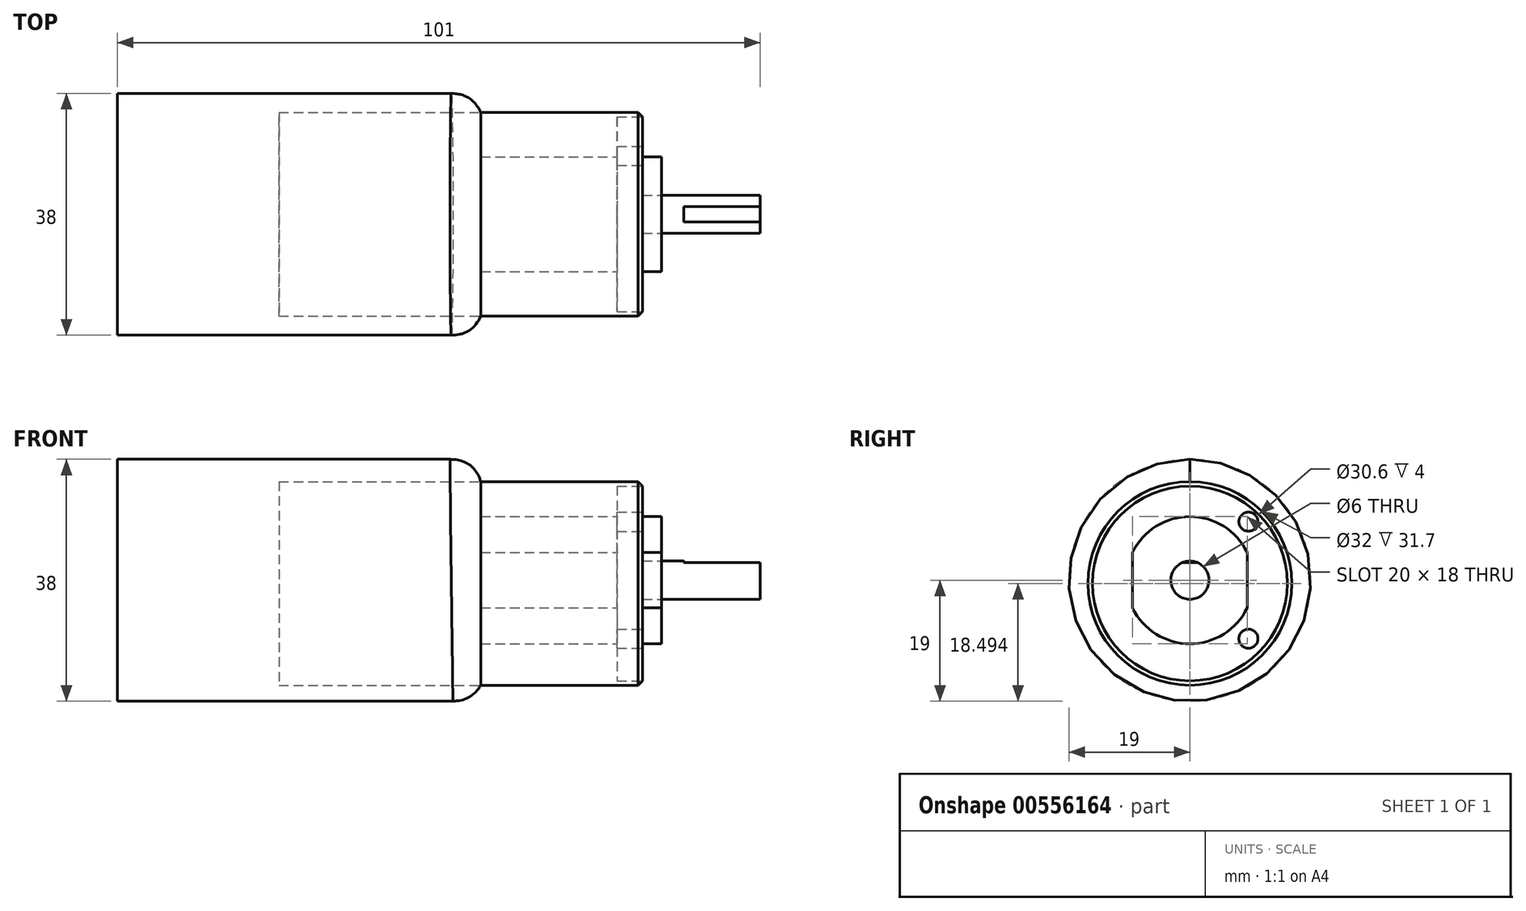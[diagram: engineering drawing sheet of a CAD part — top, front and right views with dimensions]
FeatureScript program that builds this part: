
annotation { "Feature Type Name" : "Feature", "Feature Type Description" : "" }
export const myFeature = defineFeature(function(context is Context, id is Id, definition is map)
    precondition{}
    {
        {
            var Q0;
            Q0=qCreatedBy(makeId("Right.planeOp"),FACE);
            var sketch = newSketch(context, id + "F0", { "sketchPlane" : qUnion([Q0])});
            skCircle(sketch, "E0", {"center": v(0, 0) * mm, "radius": 3 * mm});
            skSolve(sketch);
        }
        {
            var Q0;
            Q0 = qSketchRegion(id + "F0", true);
            extrude(context, id + "F1", {"entities" : qUnion([Q0]), "depth" : 15.5 * mm, "offsetDistance" : 25.4 * mm});
        }
        {
            var Q0;
            Q0=makeQuery(id+"F1.opExtrude","CAP_FACE",FACE,{"disambiguationData":[OSD([sQuery(id+"F0.wireOp",EDGE,"E0")])],"isStart":true});
            var sketch = newSketch(context, id + "F2", { "sketchPlane" : qUnion([Q0])});
            skArc(sketch, "E1", {"start": v(-9, -4.36) * mm, "mid": v(0, -10) * mm, "end": v(9, -4.36) * mm});
            skLineSegment(sketch, "E2.left", {"start": v(9, -4.36) * mm, "end": v(9, 4.36) * mm});
            skLineSegment(sketch, "E2.right", {"start": v(-9, -4.36) * mm, "end": v(-9, 4.36) * mm});
            skArc(sketch, "E3.trimOffspring", {"start": v(9, 4.36) * mm, "mid": v(0, 10) * mm, "end": v(-9, 4.36) * mm});
            skSolve(sketch);
        }
        {
            var Q0;
            Q0=makeQuery(id+"F2.imprint","IMPRINT",FACE,{"disambiguationData":[TD([[makeQuery(id+"F2.imprint","IMPRINT",EDGE,{"derivedFrom":sQuery(id+"F2.wireOp",EDGE,"E1")}),1.0]])]});
            extrude(context, id + "F3", {"entities" : qUnion([Q0]), "depth" : 3 * mm, "offsetDistance" : 25.4 * mm});
        }
        {
            var Q0;
            Q0=makeQuery(id+"F3.opExtrude","CAP_FACE",FACE,{"disambiguationData":[OSD([sQuery(id+"F0.wireOp",EDGE,"E0"),sQuery(id+"F2.wireOp",EDGE,"E1")])],"isStart":false});
            var sketch = newSketch(context, id + "F4", { "sketchPlane" : qUnion([Q0])});
            skCircle(sketch, "E4", {"center": v(0, -0.5) * mm, "radius": 16 * mm});
            skSolve(sketch);
        }
        {
            var Q0;
            Q0=makeQuery(id+"F4.imprint","IMPRINT",FACE,{"disambiguationData":[TD([[makeQuery(id+"F4.imprint","IMPRINT",EDGE,{"derivedFrom":sQuery(id+"F4.wireOp",EDGE,"E4")}),1.0]])]});
            extrude(context, id + "F5", {"entities" : qUnion([Q0]), "depth" : 25.4 * mm, "offsetDistance" : 25.4 * mm});
        }
        {
            var Q0;
            Q0=makeQuery(id+"F5.opExtrude","CAP_FACE",FACE,{"disambiguationData":[OSD([sQuery(id+"F2.wireOp",EDGE,"E1"),sQuery(id+"F4.wireOp",EDGE,"E4")])],"isStart":false});
            var sketch = newSketch(context, id + "F6", { "sketchPlane" : qUnion([Q0])});
            skCircle(sketch, "E5", {"center": v(0, 0) * mm, "radius": 19 * mm});
            skSolve(sketch);
        }
        {
            var Q0;
            Q0=makeQuery(id+"F6.imprint","IMPRINT",FACE,{"disambiguationData":[TD([[makeQuery(id+"F6.imprint","IMPRINT",EDGE,{"derivedFrom":sQuery(id+"F6.wireOp",EDGE,"E5")}),1.0]])]});
            extrude(context, id + "F7", {"entities" : qUnion([Q0]), "depth" : 57.1 * mm, "offsetDistance" : 25.4 * mm});
        }
        {
            var Q0;
            Q0=makeQuery(id+"F1.opExtrude","CAP_FACE",FACE,{"disambiguationData":[OSD([sQuery(id+"F0.wireOp",EDGE,"E0")])],"isStart":false});
            var sketch = newSketch(context, id + "F8", { "sketchPlane" : qUnion([Q0])});
            skArc(sketch, "E6", {"start": v(1.2, 2.75) * mm, "mid": v(0, 3) * mm, "end": v(-1.2, 2.75) * mm});
            skLineSegment(sketch, "E7", {"start": v(0, 2.75) * mm, "end": v(-1.2, 2.75) * mm});
            skLineSegment(sketch, "E8", {"start": v(-1.2, 2.75) * mm, "end": v(1.2, 2.75) * mm});
            skSolve(sketch);
        }
        {
            var Q0;
            Q0 = qSketchRegion(id + "F8", true);
            extrude(context, id + "F9", {"entities" : qUnion([Q0]), "operationType" : NewBodyOperationType.REMOVE, "oppositeDirection" : true, "depth" : 12 * mm, "offsetDistance" : 25.4 * mm});
        }
        {
            var Q0;
            Q0=makeQuery(id+"F7.opExtrude","CAP_FACE",FACE,{"disambiguationData":[OSD([sQuery(id+"F4.wireOp",EDGE,"E4"),sQuery(id+"F6.wireOp",EDGE,"E5")])],"isStart":false});
            var sketch = newSketch(context, id + "F10", { "sketchPlane" : qUnion([Q0])});
            skCircle(sketch, "E9", {"center": v(0, 0) * mm, "radius": 18.92 * mm});
            skSolve(sketch);
        }
        {
            var Q0;
            Q0=makeQuery(id+"F10.imprint","IMPRINT",FACE,{"disambiguationData":[TD([[makeQuery(id+"F10.imprint","IMPRINT",EDGE,{"derivedFrom":makeQuery(id+"F7.opExtrude","CAP_EDGE",EDGE,{"disambiguationData":[OSD([sQuery(id+"F4.wireOp",EDGE,"E4")])],"isStart":false})}),1.0]])]});
            extrude(context, id + "F11", {"entities" : qUnion([Q0]), "operationType" : NewBodyOperationType.ADD, "oppositeDirection" : true, "depth" : 25.4 * mm, "offsetDistance" : 25.4 * mm});
        }
        {
            var Q0;
            Q0=makeQuery(id+"F7.opExtrude","CAP_EDGE",EDGE,{"disambiguationData":[OSD([sQuery(id+"F6.wireOp",EDGE,"E5")])],"isStart":true});
            fillet(context, id + "F12", {"entities" : qUnion([Q0]), "radius" : 5.08 * mm, "tangentPropagation" : true, "rho" : 0.5, "crossSection" : FilletCrossSection.CONIC, "allowEdgeOverflow" : false});
        }
        {
            var Q0;
            Q0=makeQuery(id+"F5.opExtrude","CAP_EDGE",EDGE,{"disambiguationData":[OSD([sQuery(id+"F4.wireOp",EDGE,"E4")])],"isStart":true});
            chamfer(context, id + "F13", {"entities" : qUnion([Q0]), "width" : .7 * mm, "tangentPropagation" : true});
        }
        {
            var Q0;
            Q0=makeQuery(id+"F5.opExtrude","CAP_FACE",FACE,{"disambiguationData":[OSD([sQuery(id+"F2.wireOp",EDGE,"E1"),sQuery(id+"F2.wireOp",EDGE,"E2.left"),sQuery(id+"F2.wireOp",EDGE,"E2.right"),sQuery(id+"F2.wireOp",EDGE,"E3.trimOffspring"),sQuery(id+"F4.wireOp",EDGE,"E4")])],"isStart":true});
            var sketch = newSketch(context, id + "F14", { "sketchPlane" : qUnion([Q0])});
            skCircle(sketch, "E10", {"center": v(0, 0) * mm, "radius": 13 * mm});
            skCircle(sketch, "E11.1.0", {"center": v(-9.2, 9.2) * mm, "radius": 1.5 * mm});
            skCircle(sketch, "E11.3.0", {"center": v(-9.2, -9.2) * mm, "radius": 1.5 * mm});
            skCircle(sketch, "E11.5.0", {"center": v(9.2, -9.2) * mm, "radius": 1.5 * mm});
            skCircle(sketch, "E11.7.0", {"center": v(9.2, 9.2) * mm, "radius": 1.5 * mm});
            skPoint(sketch, "E12.center.orphan", {"position": v(0, 13) * mm});
            skSolve(sketch);
        }
        {
            var Q0;
            {var subQ0=sQuery(id+"F14.wireOp",EDGE,"E11.1.0");var subQ1=sQuery(id+"F14.wireOp",EDGE,"E10");var subQ2=makeQuery(id+"F14.imprint","INTERSECT",VERTEX,{"disambiguationData":[OD(0.0)],"derivedFrom":[subQ1,subQ0]});Q0=makeQuery(id+"F14.imprint","IMPRINT",FACE,{"disambiguationData":[TD([[makeQuery(id+"F14.imprint","IMPRINT",EDGE,{"disambiguationData":[TD([[subQ2,-1.0]])],"derivedFrom":subQ1}),-1.0]])]});}
            var Q1;
            {var subQ0=sQuery(id+"F14.wireOp",EDGE,"E11.1.0");var subQ1=sQuery(id+"F14.wireOp",EDGE,"E10");var subQ2=makeQuery(id+"F14.imprint","INTERSECT",VERTEX,{"disambiguationData":[OD(0.0)],"derivedFrom":[subQ1,subQ0]});Q1=makeQuery(id+"F14.imprint","IMPRINT",FACE,{"disambiguationData":[TD([[makeQuery(id+"F14.imprint","IMPRINT",EDGE,{"disambiguationData":[TD([[subQ2,-1.0]])],"derivedFrom":subQ1}),1.0]])]});}
            var Q2;
            {var subQ0=sQuery(id+"F14.wireOp",EDGE,"E11.7.0");var subQ1=sQuery(id+"F14.wireOp",EDGE,"E10");var subQ2=makeQuery(id+"F14.imprint","INTERSECT",VERTEX,{"disambiguationData":[OD(0.0)],"derivedFrom":[subQ1,subQ0]});Q2=makeQuery(id+"F14.imprint","IMPRINT",FACE,{"disambiguationData":[TD([[makeQuery(id+"F14.imprint","IMPRINT",EDGE,{"disambiguationData":[TD([[subQ2,1.0]])],"derivedFrom":subQ1}),1.0]])]});}
            var Q3;
            {var subQ0=sQuery(id+"F14.wireOp",EDGE,"E11.7.0");var subQ1=sQuery(id+"F14.wireOp",EDGE,"E10");var subQ2=makeQuery(id+"F14.imprint","INTERSECT",VERTEX,{"disambiguationData":[OD(0.0)],"derivedFrom":[subQ1,subQ0]});Q3=makeQuery(id+"F14.imprint","IMPRINT",FACE,{"disambiguationData":[TD([[makeQuery(id+"F14.imprint","IMPRINT",EDGE,{"disambiguationData":[TD([[subQ2,1.0]])],"derivedFrom":subQ1}),-1.0]])]});}
            var Q4;
            {var subQ0=sQuery(id+"F14.wireOp",EDGE,"E11.5.0");var subQ1=sQuery(id+"F14.wireOp",EDGE,"E10");var subQ2=makeQuery(id+"F14.imprint","INTERSECT",VERTEX,{"disambiguationData":[OD(0.0)],"derivedFrom":[subQ1,subQ0]});Q4=makeQuery(id+"F14.imprint","IMPRINT",FACE,{"disambiguationData":[TD([[makeQuery(id+"F14.imprint","IMPRINT",EDGE,{"disambiguationData":[TD([[subQ2,-1.0]])],"derivedFrom":subQ1}),-1.0]])]});}
            var Q5;
            {var subQ0=sQuery(id+"F14.wireOp",EDGE,"E11.5.0");var subQ1=sQuery(id+"F14.wireOp",EDGE,"E10");var subQ2=makeQuery(id+"F14.imprint","INTERSECT",VERTEX,{"disambiguationData":[OD(0.0)],"derivedFrom":[subQ1,subQ0]});Q5=makeQuery(id+"F14.imprint","IMPRINT",FACE,{"disambiguationData":[TD([[makeQuery(id+"F14.imprint","IMPRINT",EDGE,{"disambiguationData":[TD([[subQ2,-1.0]])],"derivedFrom":subQ1}),1.0]])]});}
            var Q6;
            {var subQ0=sQuery(id+"F14.wireOp",EDGE,"E11.3.0");var subQ1=sQuery(id+"F14.wireOp",EDGE,"E10");var subQ2=makeQuery(id+"F14.imprint","INTERSECT",VERTEX,{"disambiguationData":[OD(0.0)],"derivedFrom":[subQ1,subQ0]});Q6=makeQuery(id+"F14.imprint","IMPRINT",FACE,{"disambiguationData":[TD([[makeQuery(id+"F14.imprint","IMPRINT",EDGE,{"disambiguationData":[TD([[subQ2,-1.0]])],"derivedFrom":subQ1}),1.0]])]});}
            var Q7;
            {var subQ0=sQuery(id+"F14.wireOp",EDGE,"E11.3.0");var subQ1=sQuery(id+"F14.wireOp",EDGE,"E10");var subQ2=makeQuery(id+"F14.imprint","INTERSECT",VERTEX,{"disambiguationData":[OD(0.0)],"derivedFrom":[subQ1,subQ0]});Q7=makeQuery(id+"F14.imprint","IMPRINT",FACE,{"disambiguationData":[TD([[makeQuery(id+"F14.imprint","IMPRINT",EDGE,{"disambiguationData":[TD([[subQ2,-1.0]])],"derivedFrom":subQ1}),-1.0]])]});}
            extrude(context, id + "F15", {"entities" : qUnion([Q0, Q1, Q2, Q3, Q4, Q5, Q6, Q7]), "operationType" : NewBodyOperationType.REMOVE, "oppositeDirection" : true, "depth" : 4 * mm, "offsetDistance" : 25.4 * mm});
        }
    });
